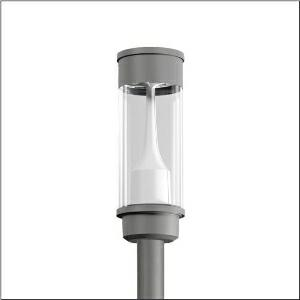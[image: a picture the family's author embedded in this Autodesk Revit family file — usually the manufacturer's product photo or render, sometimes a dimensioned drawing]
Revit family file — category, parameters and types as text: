
# Revit family: litepole_iq___pl1_2s_5xa5415rf14h_7319
name_source: partatom
category: Lighting Fixtures
units: mm (PartAtom-declared; Revit-internal decimal feet)

## family parameters
Cut with Voids When Loaded = No
Host = Face
Light Source = No
Part Type = Normal
Room Calculation Point = No
Round Connector Dimension = Use Diameter
Shared = No

## types (1)
- --- (1 x LED, 2970 lm, 18.5 W, 4000K)
    Apparent Load = 19 VA
    CIE Flux Codes = 23 62 94 96 100
    Color Rendering = 70
    Color Temperature = 4000K
    Default Elevation = 1800 mm
    Description = Litepole iQ, mast luminaire, Module 540 iQ-SR, primary light control with 3 zone facetted reflector, of plastic, silver coated, highly specular, structured, primary optical cover: cover, of PMMA, transparent, light distribution: PL1.2s, light emission: direct distribution, primary light characteristic: symmetric, installation type: post-top, LED, High Power LED, rated luminous flux: 2.970lm, luminous efficacy: 161lm/W, light colour: 740, colour temperature: 4000K, control gear: iQ Street-Remote, control: optimised constant luminous flux control (CLO 2.0), Desk-Remote (wireless, voltage-free reading and setting of iQ features in the workshop via application-optimized NFC function/RFID function), Light-Fading, Smart-Wire, Night-Set, Lumen-Switch, Temp-Guard, Auto-Match, Street-Remote, pre-setting: logarithmic dimming characteristic, with terminal, 6-pole, max. 2.5mm², mains connection: 230..240V, AC, 50/60Hz, start of lifetime: 19W, end of service life: 20W, reduction: 9W, luminaire housing, upper part, of glass-fibre reinforced polyester, coated, Siteco® metallic grey (DB 702S), diameter: 210mm, height: 590mm, spigot size: d x l = 76 x 70mm (post-top) | with reducer (optional accessory) 60 x 70mm, mounting height: 3..5m, post-top mast mounting element, of diecast aluminium, coated, Siteco® metallic grey (DB 702S), Module 540 iQ-SR, traffic white (RAL 9016), equipment: standard, protection rating (complete): IP65, insulation class (complete): insulation class II (safety insulation), certification: CE, ENEC, VDE, packaging unit: 1 piece

Light Distribution: PL1.2s
    Height = 590 mm
    Lamp = 1 x LED
    Lamp Light Flux = 2970 lm
    Lamp Power = 18.5 W
    Lamp count = 1
    Length = 220 mm
    Luminous efficacy = 161 lm/W
    Manufacturer = Siteco
    ModVariant = No
    Model = 5XA5415RF14H
    Number of Poles = 1
    OnlyDefault = Yes
    Power Factor = 1
    Product Name = Litepole iQ | PL1.2s
    Product group = mast luminaire | pylon top
    ProductGroupID = 6100
    Protection Class = Protection class II
    Protection Degree = IP 65
    RLX_Detail_Level = 1
    RLX_Emergency_Light_Flux = 0 lm
    RLX_Emergency_Type = 0
    RLX_Emergency_Type_DB = No
    RlxData = <blob elided: 39873 chars, md5=5ccf01c6>
    Socket = socket
    Standby Power = 0 W
    System Light Flux = 2970 lm
    System Power = 19 W
    Type Comments = factory setting: luminous flux: 100 % | dim-lin: 254 | 385 mA
    Type Image = l_1006025.jpg
    URL = http://relux.com
    VarID = @adj_144287
    Voltage = 0 V
    Weight = 0.00 kg
    Width = 0 mm  [stored 0 ft]

note: [stored X ft] marks values corroborated as IEEE doubles in the binary element streams (Revit-internal decimal feet)

## geometry (parser evidence)
native form markers: Blend x4, Sweep x11
no freeform markers — native parametric forms only
